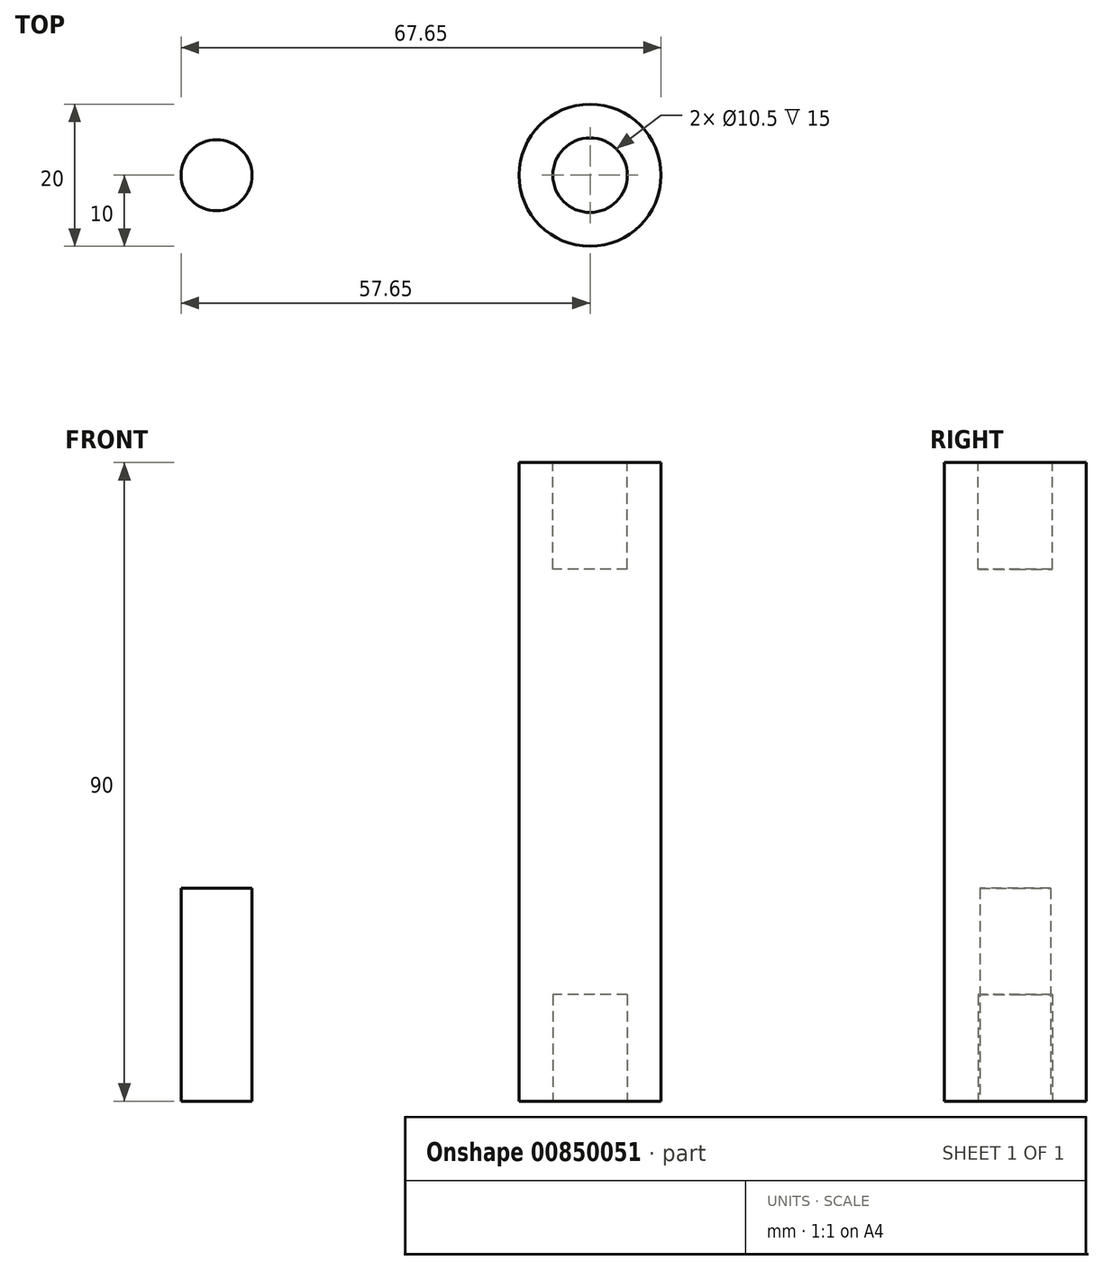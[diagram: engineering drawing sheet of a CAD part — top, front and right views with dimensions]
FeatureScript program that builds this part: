
annotation { "Feature Type Name" : "Feature", "Feature Type Description" : "" }
export const myFeature = defineFeature(function(context is Context, id is Id, definition is map)
    precondition{}
    {
        {
            var Q0;
            Q0=qCreatedBy(makeId("Top.planeOp"),FACE);
            var sketch = newSketch(context, id + "F0", { "sketchPlane" : qUnion([Q0])});
            skCircle(sketch, "E0", {"center": v(0, 0) * mm, "radius": 5.25 * mm});
            skCircle(sketch, "E1", {"center": v(0, 0) * mm, "radius": 10 * mm});
            skSolve(sketch);
        }
        {
            var Q0;
            Q0=makeQuery(id+"F0.imprint","IMPRINT",FACE,{"disambiguationData":[TD([[makeQuery(id+"F0.imprint","IMPRINT",EDGE,{"derivedFrom":sQuery(id+"F0.wireOp",EDGE,"E0")}),-1.0]])]});
            var Q1;
            Q1=makeQuery(id+"F0.imprint","IMPRINT",FACE,{"disambiguationData":[TD([[makeQuery(id+"F0.imprint","IMPRINT",EDGE,{"derivedFrom":sQuery(id+"F0.wireOp",EDGE,"E0")}),1.0]])]});
            extrude(context, id + "F1", {"entities" : qUnion([Q0, Q1]), "depth" : 45 * mm, "offsetDistance" : 25 * mm});
        }
        {
            var Q0;
            Q0=makeQuery(id+"F0.imprint","IMPRINT",FACE,{"disambiguationData":[TD([[makeQuery(id+"F0.imprint","IMPRINT",EDGE,{"derivedFrom":sQuery(id+"F0.wireOp",EDGE,"E0")}),1.0]])]});
            extrude(context, id + "F2", {"entities" : qUnion([Q0]), "operationType" : NewBodyOperationType.REMOVE, "depth" : 15 * mm, "offsetDistance" : 25 * mm});
        }
        {
            var Q0;
            Q0=makeQuery(id+"F1.opExtrude","SWEPT_BODY",BODY,{"disambiguationData":[OSD([sQuery(id+"F0.wireOp",EDGE,"E1")])]});
            var Q1;
            Q1=makeQuery(id+"F1.opExtrude","CAP_FACE",FACE,{"disambiguationData":[OSD([sQuery(id+"F0.wireOp",EDGE,"E1")])],"isStart":false});
            mirror(context, id + "F3", {"operationType" : NewBodyOperationType.ADD, "entities" : qUnion([Q0]), "mirrorPlane" : qUnion([Q1])});
        }
        {
            var Q0;
            Q0=qCreatedBy(makeId("Top.planeOp"),FACE);
            var sketch = newSketch(context, id + "F4", { "sketchPlane" : qUnion([Q0])});
            skCircle(sketch, "E2", {"center": v(-52.65, 0) * mm, "radius": 5 * mm});
            skSolve(sketch);
        }
        {
            var Q0;
            Q0 = qSketchRegion(id + "F4", true);
            extrude(context, id + "F5", {"entities" : qUnion([Q0]), "depth" : 30 * mm, "offsetDistance" : 25 * mm});
        }
    });
